# Revit family: 2-711-224 Telshor
name_source: partatom
category: Lighting Fixtures
revit_build: Autodesk Revit LT 2014 (Build: 20130308_1515(x64)
units: mm (PartAtom-declared; Revit-internal decimal feet)

## types (1)
- 2-711-224 Telshor
    ADA Compliant = Yes
    Apparent Load = 52 VA
    Color Filter = 16777215
    Default Elevation = 4' - 0"
    Description = 21.75" Comtemporary Wall Sconce
    Diffuser = Matte White Accrylic
    Dimming Lamp Color Temperature Shift = <None>
    Driver Manufacturer = Fulham
    Emit Shape Visible in Rendering = No
    Emit from Rectangle Length = 4' - 0"
    Emit from Rectangle Width = 2' - 0"
    Fixture Height = 1' - 9 5/8"
    Fixture Width = 0' - 9"
    Input Power (Watts) = 52
    Input Voltage (Volts AC) = 120
    Junction Box = 4" Octagonal
    Lamp = 2x26W Double Twin Tube Compact Fluorescent
    Lamp Manufacturer = Sylvania
    Manufacturer = Oxygen Lighting
    Metal Finsih = Satin Finish
    Model = 2-711-224
    Photometric Web File = generic
    Product Documentation Linkk = http://oxygenlighting.com.s3.amazonaws.com
    Tilt Angle = 60.00°
    Type Comments = Lighting - Fluorescent
    URL = http://www.oxygenlighting.com

## geometry (parser evidence)
native form markers: Sweep x1
no freeform markers — native parametric forms only
